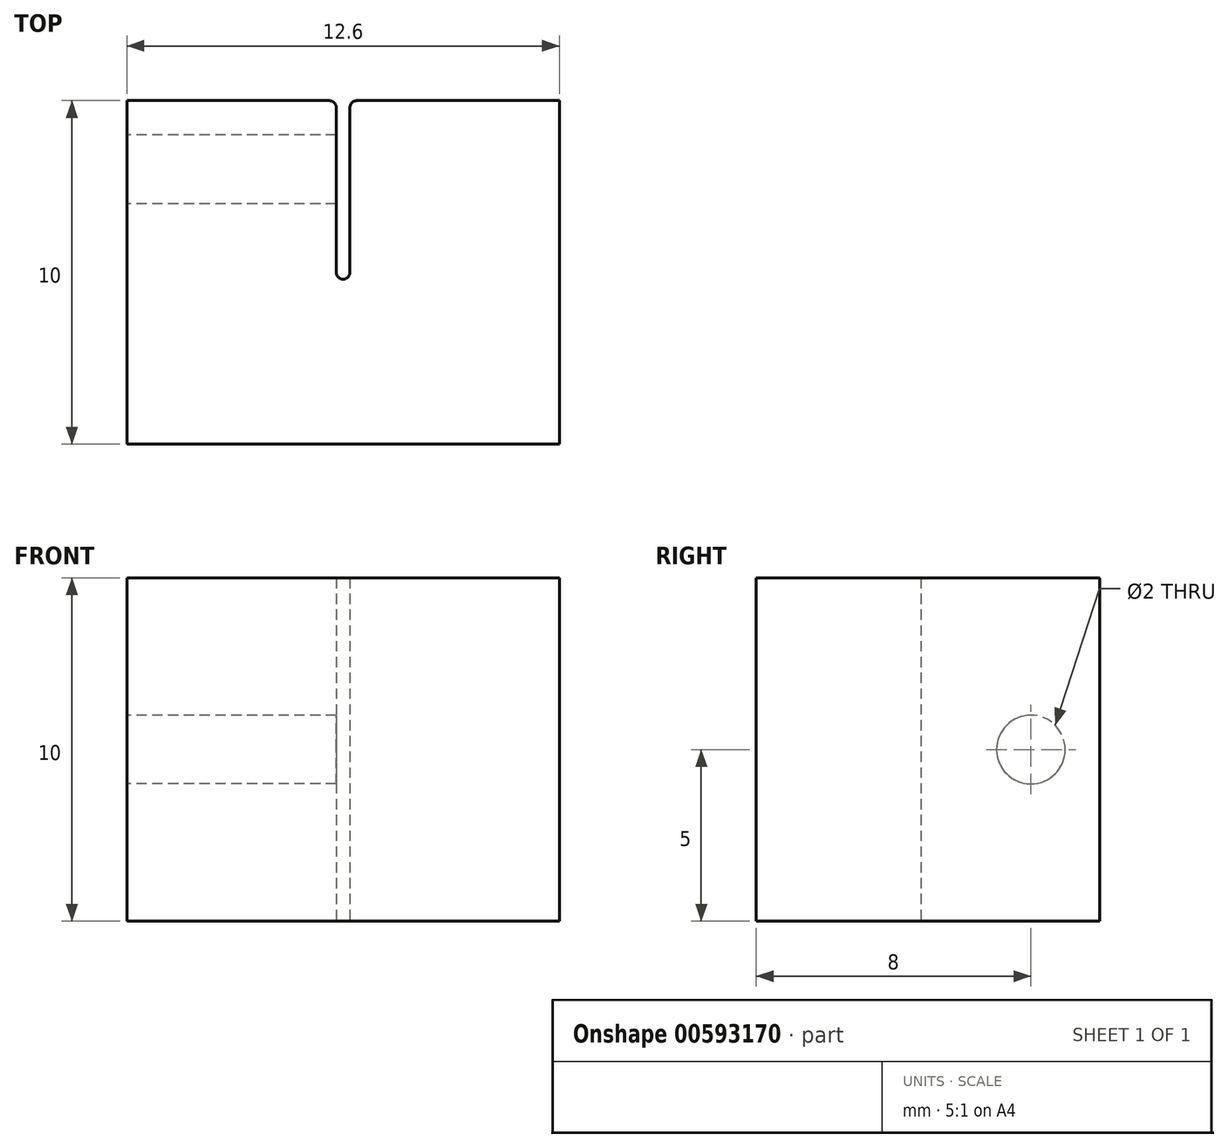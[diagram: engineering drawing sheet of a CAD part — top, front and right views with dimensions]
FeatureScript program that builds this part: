
annotation { "Feature Type Name" : "Feature", "Feature Type Description" : "" }
export const myFeature = defineFeature(function(context is Context, id is Id, definition is map)
    precondition{}
    {
        {
            var Q0;
            Q0=qCreatedBy(makeId("Top.planeOp"),FACE);
            var sketch = newSketch(context, id + "F0", { "sketchPlane" : qUnion([Q0])});
            skLineSegment(sketch, "E0.bottom", {"start": v(-6.3, 5) * mm, "end": v(-0.4, 5) * mm});
            skLineSegment(sketch, "E0.top", {"start": v(-6.3, -5) * mm, "end": v(6.3, -5) * mm});
            skLineSegment(sketch, "E0.left", {"start": v(-6.3, 5) * mm, "end": v(-6.3, -5) * mm});
            skLineSegment(sketch, "E0.right", {"start": v(6.3, 5) * mm, "end": v(6.3, -5) * mm});
            skLineSegment(sketch, "E1.top", {"start": v(0, -0.2) * mm, "end": v(0, -0.2) * mm});
            skLineSegment(sketch, "E1.left", {"start": v(-0.2, 4.8) * mm, "end": v(-0.2, 0) * mm});
            skLineSegment(sketch, "E1.right", {"start": v(0.2, 4.8) * mm, "end": v(0.2, 0) * mm});
            skLineSegment(sketch, "E2.trimOffspring", {"start": v(0.4, 5) * mm, "end": v(6.3, 5) * mm});
            skPoint(sketch, "E3.visualSharp", {"position": v(-0.2, -0.2) * mm});
            skArc(sketch, "E3.filletArc", {"start": v(-0.2, 0) * mm, "mid": v(-0.14, -0.14) * mm, "end": v(0, -0.2) * mm});
            skPoint(sketch, "E4.visualSharp", {"position": v(0.2, -0.2) * mm});
            skArc(sketch, "E4.filletArc", {"start": v(0, -0.2) * mm, "mid": v(0.14, -0.14) * mm, "end": v(0.2, 0) * mm});
            skPoint(sketch, "E5.visualSharp", {"position": v(-0.2, 5) * mm});
            skArc(sketch, "E5.filletArc", {"start": v(-0.2, 4.8) * mm, "mid": v(-0.26, 4.94) * mm, "end": v(-0.4, 5) * mm});
            skPoint(sketch, "E6.visualSharp", {"position": v(0.2, 5) * mm});
            skArc(sketch, "E6.filletArc", {"start": v(0.4, 5) * mm, "mid": v(0.26, 4.94) * mm, "end": v(0.2, 4.8) * mm});
            skSolve(sketch);
        }
        {
            var Q0;
            Q0=qSketchRegion(id+"F0",true);
            extrude(context, id + "F1", {"entities" : qUnion([Q0]), "depth" : 10 * mm, "offsetDistance" : 25 * mm});
        }
        {
            var Q0;
            Q0=makeQuery(id+"F1.opExtrude","SWEPT_FACE",FACE,{"disambiguationData":[OSD([sQuery(id+"F0.wireOp",EDGE,"E0.left")])]});
            var sketch = newSketch(context, id + "F2", { "sketchPlane" : qUnion([Q0])});
            skCircle(sketch, "E7", {"center": v(-3, 5) * mm, "radius": 1 * mm});
            skSolve(sketch);
        }
        {
            var Q0;
            Q0 = qSketchRegion(id + "F2", true);
            extrude(context, id + "F3", {"entities" : qUnion([Q0]), "operationType" : NewBodyOperationType.REMOVE, "oppositeDirection" : true, "depth" : 6.2 * mm, "offsetDistance" : 25 * mm});
        }
    });
